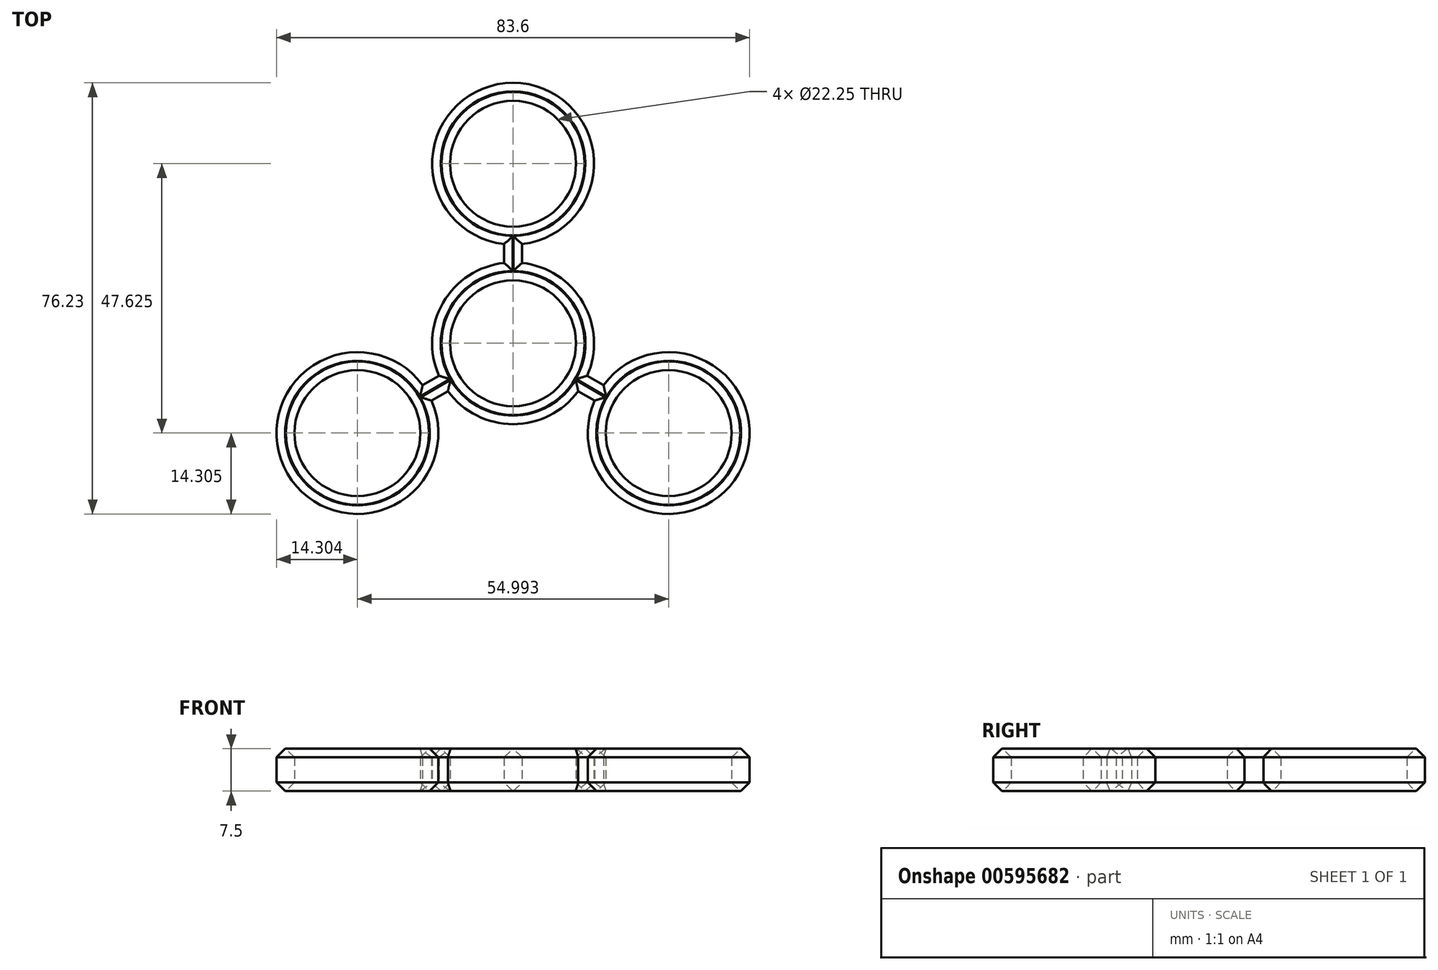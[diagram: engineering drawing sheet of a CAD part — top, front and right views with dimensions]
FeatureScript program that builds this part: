
annotation { "Feature Type Name" : "Feature", "Feature Type Description" : "" }
export const myFeature = defineFeature(function(context is Context, id is Id, definition is map)
    precondition{}
    {
        {
            var Q0;
            Q0=qCreatedBy(makeId("Top.planeOp"),FACE);
            var sketch = newSketch(context, id + "F0", { "sketchPlane" : qUnion([Q0])});
            skCircle(sketch, "E0", {"center": v(0, 0) * mm, "radius": 11.12 * mm});
            skCircle(sketch, "E1", {"center": v(0, 0) * mm, "radius": 14.3 * mm});
            skCircle(sketch, "E2", {"center": v(0, 31.75) * mm, "radius": 11.12 * mm});
            skCircle(sketch, "E3", {"center": v(0, 31.75) * mm, "radius": 14.3 * mm});
            skLineSegment(sketch, "E4.bottom", {"start": v(-1.59, 12.71) * mm, "end": v(1.59, 12.71) * mm});
            skLineSegment(sketch, "E4.top", {"start": v(-1.59, 19.04) * mm, "end": v(1.59, 19.04) * mm});
            skLineSegment(sketch, "E4.left", {"start": v(-1.59, 12.71) * mm, "end": v(-1.59, 19.04) * mm});
            skLineSegment(sketch, "E4.right", {"start": v(1.59, 12.71) * mm, "end": v(1.59, 19.04) * mm});
            skPoint(sketch, "E4.middle", {"position": v(0, 15.88) * mm});
            skCircle(sketch, "E5.1.0", {"center": v(-27.5, -15.87) * mm, "radius": 14.3 * mm});
            skCircle(sketch, "E5.1.1", {"center": v(-27.5, -15.87) * mm, "radius": 11.12 * mm});
            skLineSegment(sketch, "E5.1.2", {"start": v(-11.8, -4.98) * mm, "end": v(-17.28, -8.14) * mm});
            skLineSegment(sketch, "E5.1.3", {"start": v(-10.22, -7.73) * mm, "end": v(-15.7, -10.9) * mm});
            skLineSegment(sketch, "E5.1.4", {"start": v(-15.7, -10.9) * mm, "end": v(-17.28, -8.14) * mm});
            skLineSegment(sketch, "E5.1.5", {"start": v(-10.22, -7.73) * mm, "end": v(-11.8, -4.98) * mm});
            skCircle(sketch, "E5.2.0", {"center": v(27.5, -15.88) * mm, "radius": 14.3 * mm});
            skCircle(sketch, "E5.2.1", {"center": v(27.5, -15.88) * mm, "radius": 11.12 * mm});
            skLineSegment(sketch, "E5.2.2", {"start": v(10.22, -7.73) * mm, "end": v(15.7, -10.9) * mm});
            skLineSegment(sketch, "E5.2.3", {"start": v(11.8, -4.98) * mm, "end": v(17.28, -8.14) * mm});
            skLineSegment(sketch, "E5.2.4", {"start": v(17.28, -8.14) * mm, "end": v(15.7, -10.9) * mm});
            skLineSegment(sketch, "E5.2.5", {"start": v(11.8, -4.98) * mm, "end": v(10.22, -7.73) * mm});
            skSolve(sketch);
        }
        {
            var Q0;
            Q0 = qSketchRegion(id + "F0", true);
            extrude(context, id + "F1", {"entities" : qUnion([Q0]), "depth" : 7.5 * mm, "offsetDistance" : 25.4 * mm});
        }
        {
            var Q0;
            Q0=makeQuery(id+"F1.opExtrude","CAP_FACE",FACE,{"disambiguationData":[OSD([sQuery(id+"F0.wireOp",EDGE,"E0"),sQuery(id+"F0.wireOp",EDGE,"E1"),sQuery(id+"F0.wireOp",EDGE,"E2"),sQuery(id+"F0.wireOp",EDGE,"E3"),sQuery(id+"F0.wireOp",EDGE,"E4.left"),sQuery(id+"F0.wireOp",EDGE,"E4.right"),sQuery(id+"F0.wireOp",EDGE,"E5.1.0"),sQuery(id+"F0.wireOp",EDGE,"E5.1.1"),sQuery(id+"F0.wireOp",EDGE,"E5.1.2"),sQuery(id+"F0.wireOp",EDGE,"E5.1.3"),sQuery(id+"F0.wireOp",EDGE,"E5.2.0"),sQuery(id+"F0.wireOp",EDGE,"E5.2.1"),sQuery(id+"F0.wireOp",EDGE,"E5.2.2"),sQuery(id+"F0.wireOp",EDGE,"E5.2.3")])],"isStart":false});
            var Q1;
            Q1=makeQuery(id+"F1.opExtrude","CAP_FACE",FACE,{"disambiguationData":[OSD([sQuery(id+"F0.wireOp",EDGE,"E0"),sQuery(id+"F0.wireOp",EDGE,"E1"),sQuery(id+"F0.wireOp",EDGE,"E2"),sQuery(id+"F0.wireOp",EDGE,"E3"),sQuery(id+"F0.wireOp",EDGE,"E4.left"),sQuery(id+"F0.wireOp",EDGE,"E4.right"),sQuery(id+"F0.wireOp",EDGE,"E5.1.0"),sQuery(id+"F0.wireOp",EDGE,"E5.1.1"),sQuery(id+"F0.wireOp",EDGE,"E5.1.2"),sQuery(id+"F0.wireOp",EDGE,"E5.1.3"),sQuery(id+"F0.wireOp",EDGE,"E5.2.0"),sQuery(id+"F0.wireOp",EDGE,"E5.2.1"),sQuery(id+"F0.wireOp",EDGE,"E5.2.2"),sQuery(id+"F0.wireOp",EDGE,"E5.2.3")])],"isStart":true});
            chamfer(context, id + "F2", {"entities" : qUnion([Q0, Q1]), "width" : 1.52 * mm, "tangentPropagation" : true});
        }
    });
